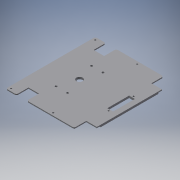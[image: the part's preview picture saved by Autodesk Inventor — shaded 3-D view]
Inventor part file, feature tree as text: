
AUTODESK INVENTOR PART (.ipt)
format: ipt  version: 2016 (Build 200138000, 138)  size: 263,680 bytes
history: native  units: in
note: dims shown in document units (in); Inventor stores cm internally (conversion verified against a paired STEP export)
features: extrude x6, sketch x6, fillet x1
ambient origin geometry x8: Origin, YZ Plane, XZ Plane, XY Plane, X Axis, Y Axis, Z Axis, Center Point
bodies: Solid1 (feature_tree)
feature tree (13):
  extrude  "Extrusion1"  Depth=0.0394in
  extrude  "Extrusion2"  Depth=0.0394in
  extrude  "Extrusion3"  Depth=0.0394in
  extrude  "Extrusion4"  Depth=0.0787in TaperAngle=0.0deg
  extrude  "Extrusion5"  Depth=0.1181in
  fillet  "Fillet1"  Radius=0.1181in
  extrude  "Extrusion7"  Depth=0.1181in
  sketch  "Sketch1"  dims[d0=0.0394in d1=0.0394in]
  sketch  "Sketch4"  dims[d2=0.0394in d3=0.0394in]
  sketch  "Sketch5"  dims[d4=0.0394in d5=0.0394in]
  sketch  "Sketch8"  dims[d6=0.0394in d8=0.0787in d9=0.0in]
  sketch  "Sketch9"  dims[d40=0.0787in d53=0.1181in d54=0.1181in]
  sketch  "Sketch13"  dims[d55=0.1181in d56=0.1181in d57=0.1181in d58=0.1181in d59=0.2756in d60=0.1181in d61=0.1181in d62=0.1181in d63=0.2756in d65=0.0787in d66=0.0in d67=0.1575in d68=0.0in d71=0.4724in d72=0.5512in d73=0.1772in d74=0.1575in d75=1.3386in d76=0.1575in d77=2.7921in d78=0.7874in d79=0.1575in d80=3.3465in d82=0.1969in d83=0.0in d84=0.2362in d85=0.2362in d86=0.1181in d87=0.1181in d88=0.1181in d89=0.2362in d90=0.1181in d91=0.2362in d92=0.4331in d93=0.0in d94=0.1181in d97=0.0394in d99=3.3071in d100=0.9843in d101=1.063in d102=0.0394in d103=5.7874in d104=0.0394in d117=0.7087in d118=0.7874in d119=0.3937in d120=0.0in]
